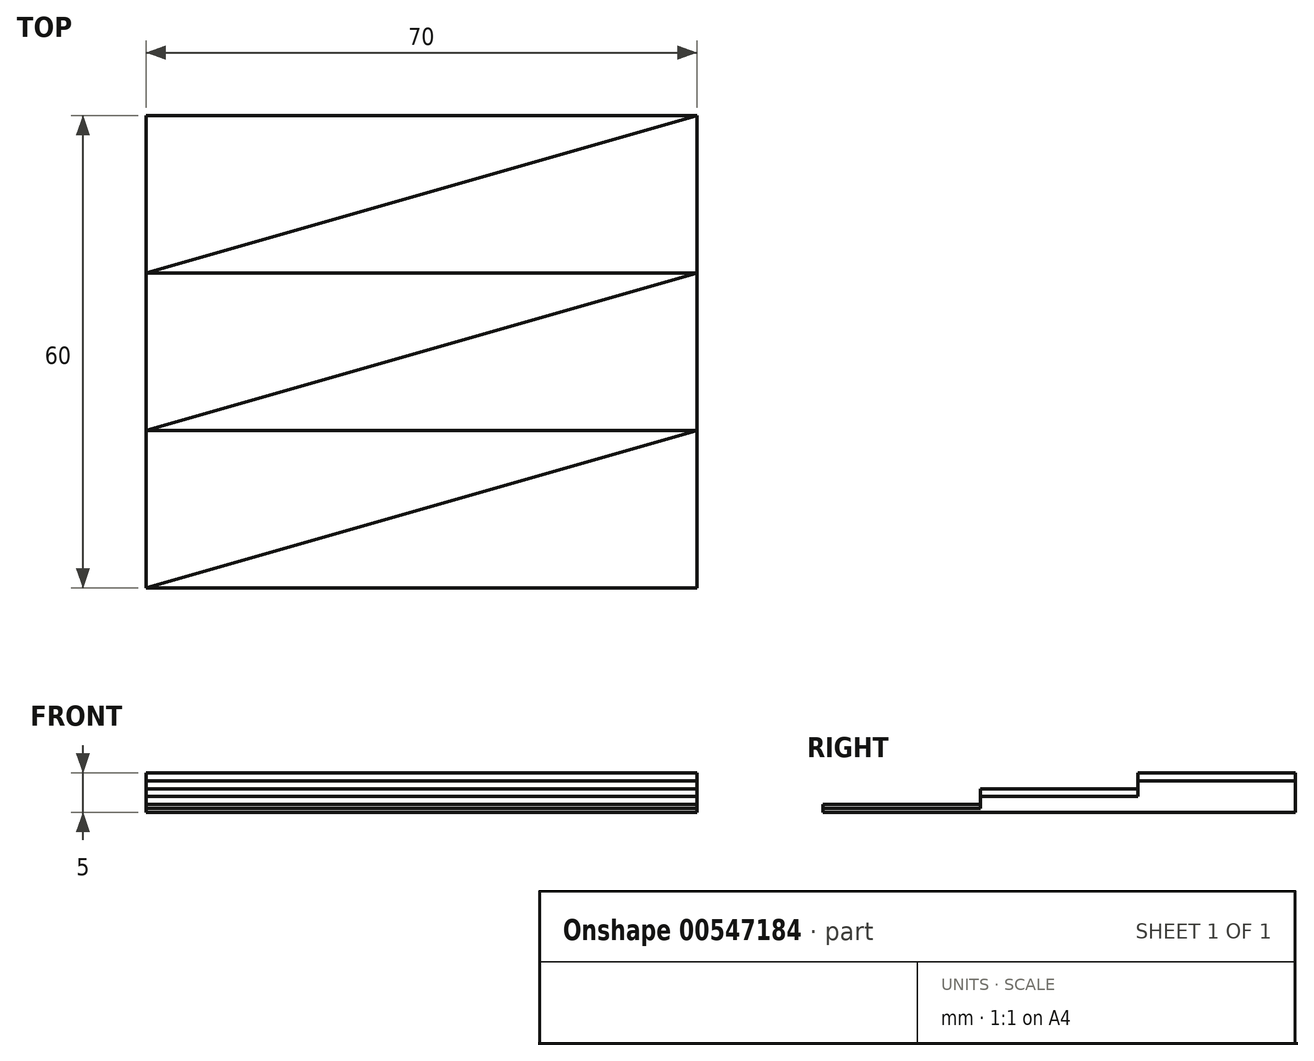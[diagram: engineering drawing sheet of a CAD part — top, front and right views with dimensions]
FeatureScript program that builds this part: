
annotation { "Feature Type Name" : "Feature", "Feature Type Description" : "" }
export const myFeature = defineFeature(function(context is Context, id is Id, definition is map)
    precondition{}
    {
        {
            var Q0;
            Q0=qCreatedBy(makeId("Top.planeOp"),FACE);
            var sketch = newSketch(context, id + "F0", { "sketchPlane" : qUnion([Q0])});
            skLineSegment(sketch, "E0.bottom", {"start": v(-33.32, 0) * mm, "end": v(36.68, 0) * mm});
            skLineSegment(sketch, "E0.top", {"start": v(-33.32, -130) * mm, "end": v(36.68, -130) * mm});
            skLineSegment(sketch, "E0.left", {"start": v(-33.32, 0) * mm, "end": v(-33.32, -130) * mm});
            skLineSegment(sketch, "E0.right", {"start": v(36.68, 0) * mm, "end": v(36.68, -130) * mm});
            skLineSegment(sketch, "E1", {"start": v(-33.32, -130) * mm, "end": v(36.68, -110) * mm});
            skLineSegment(sketch, "E2", {"start": v(36.68, -110) * mm, "end": v(-33.32, -110) * mm});
            skLineSegment(sketch, "E3", {"start": v(-33.32, -110) * mm, "end": v(36.68, -90) * mm});
            skLineSegment(sketch, "E4", {"start": v(36.68, -90) * mm, "end": v(-33.32, -90) * mm});
            skLineSegment(sketch, "E5", {"start": v(-33.32, -90) * mm, "end": v(36.68, -70) * mm});
            skLineSegment(sketch, "E6", {"start": v(36.68, -70) * mm, "end": v(-33.32, -70) * mm});
            skSolve(sketch);
        }
        {
            var Q0;
            {var subQ0=sQuery(id+"F0.wireOp",EDGE,"E0.top");Q0=makeQuery(id+"F0.imprint","IMPRINT",FACE,{"disambiguationData":[TD([[makeQuery(id+"F0.imprint","IMPRINT",EDGE,{"derivedFrom":subQ0}),1.0]])]});}
            extrude(context, id + "F1", {"entities" : qUnion([Q0]), "depth" : 0.5 * mm, "offsetDistance" : 25 * mm});
        }
        {
            var Q0;
            {var subQ0=sQuery(id+"F0.wireOp",EDGE,"E1");Q0=makeQuery(id+"F0.imprint","IMPRINT",FACE,{"disambiguationData":[TD([[makeQuery(id+"F0.imprint","IMPRINT",EDGE,{"derivedFrom":subQ0}),1.0]])]});}
            extrude(context, id + "F2", {"entities" : qUnion([Q0]), "operationType" : NewBodyOperationType.ADD, "depth" : 1 * mm, "offsetDistance" : 25 * mm});
        }
        {
            var Q0;
            {var subQ0=sQuery(id+"F0.wireOp",EDGE,"E2");Q0=makeQuery(id+"F0.imprint","IMPRINT",FACE,{"disambiguationData":[TD([[makeQuery(id+"F0.imprint","IMPRINT",EDGE,{"derivedFrom":subQ0}),-1.0]])]});}
            extrude(context, id + "F3", {"entities" : qUnion([Q0]), "operationType" : NewBodyOperationType.ADD, "depth" : 2 * mm, "offsetDistance" : 25 * mm});
        }
        {
            var Q0;
            {var subQ0=sQuery(id+"F0.wireOp",EDGE,"E3");Q0=makeQuery(id+"F0.imprint","IMPRINT",FACE,{"disambiguationData":[TD([[makeQuery(id+"F0.imprint","IMPRINT",EDGE,{"derivedFrom":subQ0}),1.0]])]});}
            extrude(context, id + "F4", {"entities" : qUnion([Q0]), "operationType" : NewBodyOperationType.ADD, "depth" : 3 * mm, "offsetDistance" : 25 * mm});
        }
        {
            var Q0;
            {var subQ0=sQuery(id+"F0.wireOp",EDGE,"E4");Q0=makeQuery(id+"F0.imprint","IMPRINT",FACE,{"disambiguationData":[TD([[makeQuery(id+"F0.imprint","IMPRINT",EDGE,{"derivedFrom":subQ0}),-1.0]])]});}
            extrude(context, id + "F5", {"entities" : qUnion([Q0]), "operationType" : NewBodyOperationType.ADD, "depth" : 4 * mm, "offsetDistance" : 25 * mm});
        }
        {
            var Q0;
            {var subQ0=sQuery(id+"F0.wireOp",EDGE,"E5");Q0=makeQuery(id+"F0.imprint","IMPRINT",FACE,{"disambiguationData":[TD([[makeQuery(id+"F0.imprint","IMPRINT",EDGE,{"derivedFrom":subQ0}),1.0]])]});}
            extrude(context, id + "F6", {"entities" : qUnion([Q0]), "operationType" : NewBodyOperationType.ADD, "depth" : 5 * mm, "offsetDistance" : 25 * mm});
        }
    });
